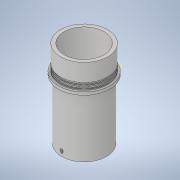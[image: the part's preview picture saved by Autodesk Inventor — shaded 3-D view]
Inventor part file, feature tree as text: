
AUTODESK INVENTOR PART (.ipt)
format: ipt  version: 2022 (Build 260153000, 153)  size: 235,008 bytes
history: native  units: mm
features: sketch x13, extrude x7, plane x6, hole x4, fillet x2, chamfer x1
ambient origin geometry x8: Origin, YZ Plane, XZ Plane, XY Plane, X Axis, Y Axis, Z Axis, Center Point
bodies: Volumenkörper1 (feature_tree)
feature tree (33):
  extrude  "Extrusion1"  Depth=90.0mm TaperAngle=0.0deg
  extrude  "Extrusion2"  Depth=43.0mm
  plane  "Arbeitsebene1"
  extrude  "Extrusion3"  [1 undecoded]
  plane  "Arbeitsebene2"
  extrude  "Extrusion4"  Depth=3.0mm TaperAngle=0.0deg
  plane  "Arbeitsebene3"
  extrude  "Extrusion5"  Depth=46.4mm
  fillet  "Rundung1"  Radius=2.2mm
  fillet  "Rundung2"  Radius=4.6mm
  hole  "Bohrung2"  [1 undecoded]
  hole  "Bohrung4"  [1 undecoded]
  chamfer  "Fase2"  Distance=0.5mm Angle=45.0deg
  hole  "Bohrung5"  [1 undecoded]
  sketch  "Skizze16"  dims[d68=30.0mm d69=6.0mm d70=4.0mm d71=2.0mm d72=90.0deg d73=5.0mm d74=0.0mm d75=45.0deg]
  plane  "Arbeitsebene7"
  plane  "Arbeitsebene9"
  sketch  "Skizze17"  dims[d76=3.0mm d77=3.0mm d78=4.0mm d79=2.0mm d80=90.0deg d81=4.0mm d82=0.0mm d83=4.0mm]
  hole  "Bohrung6"  [1 undecoded]
  extrude  "Extrusion8"  Depth=10.0mm TaperAngle=0.0deg
  plane  "Arbeitsebene10"
  extrude  "Extrusion9"  Depth=43.5mm
  sketch  "Skizze1"  dims[d0=48.8mm d1=90.0mm d2=0.0mm]
  sketch  "Skizze3"  dims[d14=41.4mm d15=6.0mm d16=4.0mm d17=2.0mm d18=90.0deg d19=80.0mm d20=0.0mm d21=43.0mm]
  sketch  "Skizze5"  dims[d22=10.0mm d23=0.0mm d24=-65.0mm]
  sketch  "Skizze6"  dims[d25=53.0mm d26=3.0mm d27=0.0mm]
  sketch  "Skizze7"  dims[d28=1.0mm d29=46.4mm d30=2.2mm d31=0.0mm d32=4.6mm]
  sketch  "Skizze8"  dims[d33=46.4mm d34=2.2mm d35=0.0mm]
  sketch  "Skizze14"  dims[d36=0.2mm d37=0.3mm]
  sketch  "Skizze15"  dims[d58=16.2mm d59=6.0mm d60=4.0mm d61=2.0mm d62=90.0deg d63=10.0mm d64=0.0mm d65=0.5mm d66=2.0mm d67=45.0deg]
  sketch  "Skizze18"  dims[d84=46.5mm d85=10.0mm d86=0.0mm]
  sketch  "Skizze19"  dims[d87=-3.0mm d88=43.5mm]
  sketch  "Skizze20"  dims[d89=1.8mm d90=0.0mm d91=76.5mm d92=0.5mm d93=0.872665mm d94=0.5mm d95=0.872665mm]
note: 5 required parameter values undecoded (feature->parameter linkage not recoverable at this tier; creation-order binding heuristic only, values carry confidence <= 0.55)
